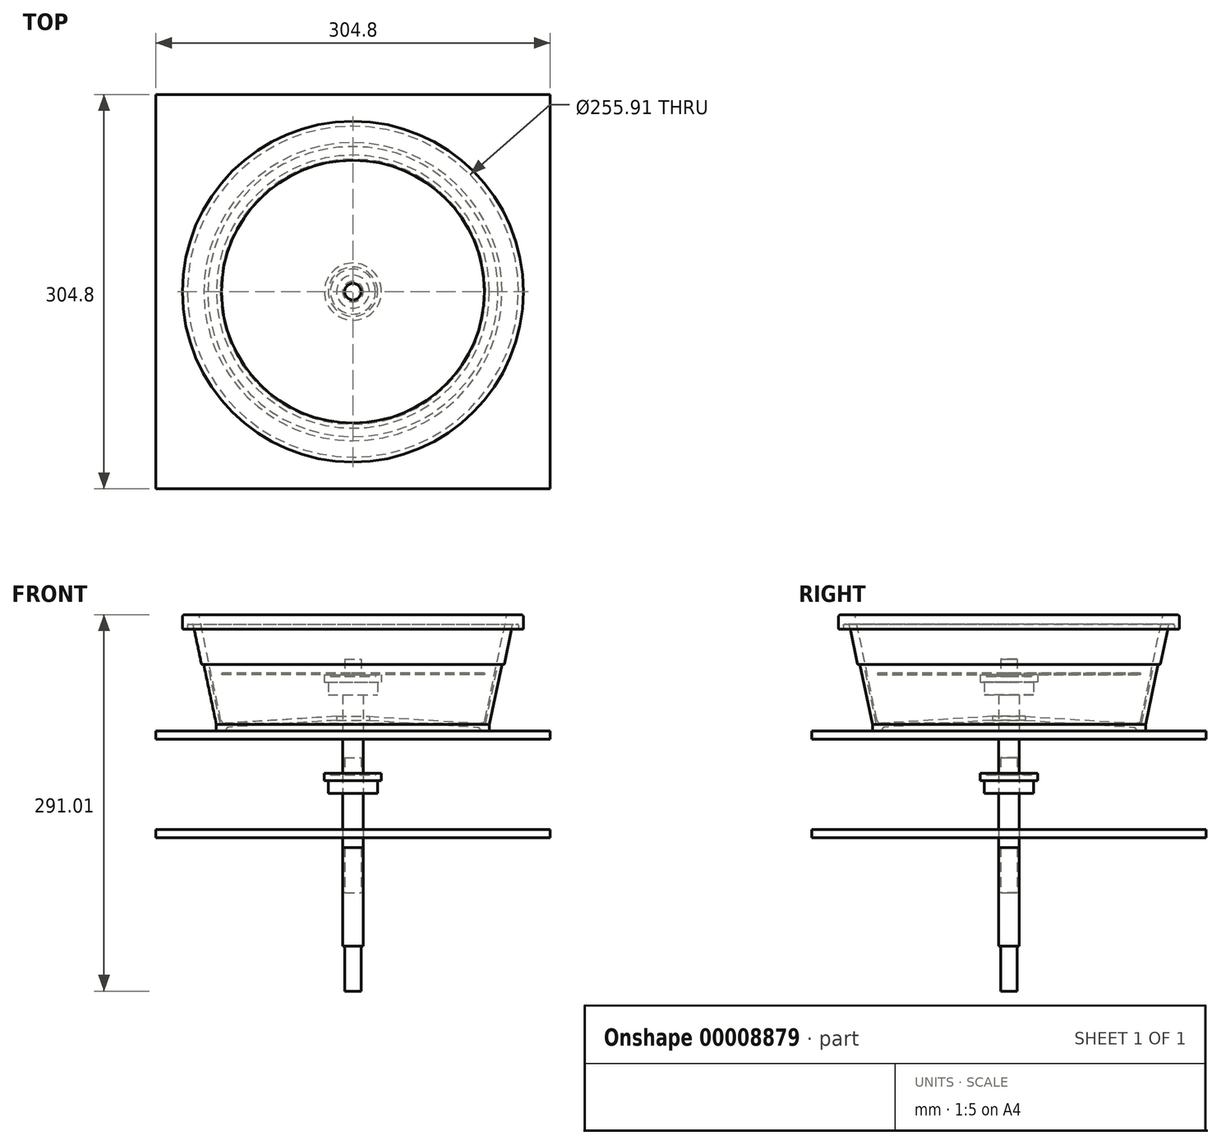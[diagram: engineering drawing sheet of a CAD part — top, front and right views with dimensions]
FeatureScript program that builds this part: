
annotation { "Feature Type Name" : "Feature", "Feature Type Description" : "" }
export const myFeature = defineFeature(function(context is Context, id is Id, definition is map)
    precondition{}
    {
        {
            var Q0;
            Q0=qCreatedBy(makeId("Front.planeOp"),FACE);
            var sketch = newSketch(context, id + "F0", { "sketchPlane" : qUnion([Q0])});
            skLineSegment(sketch, "E0", {"start": v(0, 0) * mm, "end": v(96.23, -6.08) * mm});
            skLineSegment(sketch, "E1", {"start": v(98.98, -8.76) * mm, "end": v(96.77, -6.33) * mm});
            skLineSegment(sketch, "E2", {"start": v(99.57, -9.02) * mm, "end": v(104.77, -9.02) * mm});
            skLineSegment(sketch, "E3", {"start": v(105.57, -8.22) * mm, "end": v(105.57, -3.94) * mm});
            skLineSegment(sketch, "E4", {"start": v(115.12, 41.79) * mm, "end": v(105.57, -3.94) * mm});
            skLineSegment(sketch, "E5", {"start": v(115.9, 42.42) * mm, "end": v(116.39, 42.42) * mm});
            skLineSegment(sketch, "E6", {"start": v(117.16, 43.05) * mm, "end": v(123.38, 72.77) * mm});
            skLineSegment(sketch, "E7", {"start": v(124.15, 73.4) * mm, "end": v(127.16, 73.4) * mm});
            skLineSegment(sketch, "E8", {"start": v(127.95, 72.61) * mm, "end": v(127.95, 70.39) * mm});
            skLineSegment(sketch, "E9", {"start": v(128.75, 69.6) * mm, "end": v(130.97, 69.6) * mm});
            skLineSegment(sketch, "E10", {"start": v(131.76, 70.39) * mm, "end": v(131.76, 79.18) * mm});
            skLineSegment(sketch, "E11", {"start": v(130.18, 80.77) * mm, "end": v(119.7, 80.77) * mm});
            skLineSegment(sketch, "E12", {"start": v(118.93, 80.14) * mm, "end": v(102.05, -0.66) * mm});
            skLineSegment(sketch, "E13", {"start": v(98.74, -3.18) * mm, "end": v(0, 3.05) * mm});
            skLineSegment(sketch, "E14", {"start": v(0, 3.05) * mm, "end": v(0, 0) * mm});
            skLineSegment(sketch, "E15", {"start": v(0, 0) * mm, "end": v(0, -9.02) * mm, "construction": true});
            skLineSegment(sketch, "E16", {"start": v(-105.57, -9.02) * mm, "end": v(105.57, -9.02) * mm, "construction": true});
            skLineSegment(sketch, "E17", {"start": v(0, 0) * mm, "end": v(0, 80.77) * mm, "construction": true});
            skLineSegment(sketch, "E18", {"start": v(-131.76, 80.77) * mm, "end": v(131.76, 80.77) * mm, "construction": true});
            skPoint(sketch, "E19.visualSharp", {"position": v(131.76, 80.77) * mm});
            skArc(sketch, "E19.filletArc", {"start": v(131.76, 79.18) * mm, "mid": v(131.3, 80.3) * mm, "end": v(130.18, 80.77) * mm});
            skPoint(sketch, "E20.visualSharp", {"position": v(119.06, 80.77) * mm});
            skArc(sketch, "E20.filletArc", {"start": v(119.7, 80.77) * mm, "mid": v(119.2, 80.6) * mm, "end": v(118.93, 80.14) * mm});
            skPoint(sketch, "E21.visualSharp", {"position": v(131.76, 69.6) * mm});
            skArc(sketch, "E21.filletArc", {"start": v(130.97, 69.6) * mm, "mid": v(131.53, 69.83) * mm, "end": v(131.76, 70.39) * mm});
            skPoint(sketch, "E22.visualSharp", {"position": v(127.95, 69.6) * mm});
            skArc(sketch, "E22.filletArc", {"start": v(127.95, 70.39) * mm, "mid": v(128.18, 69.83) * mm, "end": v(128.75, 69.6) * mm});
            skPoint(sketch, "E23.visualSharp", {"position": v(127.95, 73.4) * mm});
            skArc(sketch, "E23.filletArc", {"start": v(127.95, 72.61) * mm, "mid": v(127.72, 73.17) * mm, "end": v(127.16, 73.4) * mm});
            skPoint(sketch, "E24.visualSharp", {"position": v(123.5, 73.4) * mm});
            skArc(sketch, "E24.filletArc", {"start": v(124.15, 73.4) * mm, "mid": v(123.65, 73.23) * mm, "end": v(123.38, 72.77) * mm});
            skPoint(sketch, "E25.visualSharp", {"position": v(117.03, 42.42) * mm});
            skArc(sketch, "E25.filletArc", {"start": v(116.39, 42.42) * mm, "mid": v(116.89, 42.6) * mm, "end": v(117.16, 43.05) * mm});
            skPoint(sketch, "E26.visualSharp", {"position": v(115.25, 42.42) * mm});
            skArc(sketch, "E26.filletArc", {"start": v(115.9, 42.42) * mm, "mid": v(115.4, 42.24) * mm, "end": v(115.12, 41.79) * mm});
            skPoint(sketch, "E27.visualSharp", {"position": v(105.57, -9.02) * mm});
            skArc(sketch, "E27.filletArc", {"start": v(104.77, -9.02) * mm, "mid": v(105.34, -8.78) * mm, "end": v(105.57, -8.22) * mm});
            skPoint(sketch, "E28.visualSharp", {"position": v(99.22, -9.02) * mm});
            skArc(sketch, "E28.filletArc", {"start": v(98.98, -8.76) * mm, "mid": v(99.25, -8.95) * mm, "end": v(99.57, -9.02) * mm});
            skPoint(sketch, "E29.visualSharp", {"position": v(96.55, -6.1) * mm});
            skArc(sketch, "E29.filletArc", {"start": v(96.77, -6.33) * mm, "mid": v(96.52, -6.15) * mm, "end": v(96.23, -6.08) * mm});
            skPoint(sketch, "E30.visualSharp", {"position": v(101.48, -3.35) * mm});
            skArc(sketch, "E30.filletArc", {"start": v(98.74, -3.18) * mm, "mid": v(100.86, -2.54) * mm, "end": v(102.05, -0.66) * mm});
            skSolve(sketch);
        }
        {
            var Q0;
            Q0=makeQuery(id+"F0.imprint","IMPRINT",FACE,{"disambiguationData":[TD([[makeQuery(id+"F0.imprint","IMPRINT",EDGE,{"derivedFrom":sQuery(id+"F0.wireOp",EDGE,"E0")}),1.0]])]});
            var Q1;
            Q1=sQuery(id+"F0.wireOp",EDGE,"E17");
            revolve(context, id + "F1", {"entities" : qUnion([Q0]), "axis" : qUnion([Q1]), "revolveType" : RevolveType.FULL});
        }
        {
            var Q0;
            Q0=qCreatedBy(makeId("Front.planeOp"),FACE);
            var sketch = newSketch(context, id + "F2", { "sketchPlane" : qUnion([Q0])});
            skLineSegment(sketch, "E31", {"start": v(0, 0) * mm, "end": v(96.23, -6.08) * mm});
            skLineSegment(sketch, "E32", {"start": v(98.98, -8.76) * mm, "end": v(96.77, -6.33) * mm});
            skLineSegment(sketch, "E33", {"start": v(99.57, -9.02) * mm, "end": v(104.78, -9.02) * mm});
            skLineSegment(sketch, "E34", {"start": v(105.57, -8.22) * mm, "end": v(105.57, -3.94) * mm});
            skLineSegment(sketch, "E35", {"start": v(115.29, 42.42) * mm, "end": v(105.57, -3.94) * mm});
            skLineSegment(sketch, "E36", {"start": v(102.56, -3.42) * mm, "end": v(0, 3.05) * mm});
            skLineSegment(sketch, "E37", {"start": v(0, 3.05) * mm, "end": v(0, 0) * mm});
            skLineSegment(sketch, "E38", {"start": v(0, 0) * mm, "end": v(0, -9.02) * mm, "construction": true});
            skLineSegment(sketch, "E39", {"start": v(-105.57, -9.02) * mm, "end": v(105.57, -9.02) * mm, "construction": true});
            skLineSegment(sketch, "E40", {"start": v(0, 0) * mm, "end": v(0, 80.77) * mm, "construction": true});
            skPoint(sketch, "E41.visualSharp", {"position": v(105.57, -9.02) * mm});
            skArc(sketch, "E41.filletArc", {"start": v(104.78, -9.02) * mm, "mid": v(105.34, -8.78) * mm, "end": v(105.57, -8.22) * mm});
            skPoint(sketch, "E42.visualSharp", {"position": v(99.22, -9.02) * mm});
            skArc(sketch, "E42.filletArc", {"start": v(98.98, -8.76) * mm, "mid": v(99.25, -8.95) * mm, "end": v(99.57, -9.02) * mm});
            skPoint(sketch, "E43.visualSharp", {"position": v(96.55, -6.1) * mm});
            skArc(sketch, "E43.filletArc", {"start": v(96.77, -6.33) * mm, "mid": v(96.52, -6.15) * mm, "end": v(96.23, -6.08) * mm});
            skLineSegment(sketch, "E44", {"start": v(112.17, 42.42) * mm, "end": v(115.29, 42.42) * mm});
            skLineSegment(sketch, "E45", {"start": v(112.17, 42.42) * mm, "end": v(102.56, -3.42) * mm});
            skSolve(sketch);
        }
        {
            var Q0;
            Q0=makeQuery(id+"F2.imprint","IMPRINT",FACE,{"disambiguationData":[TD([[makeQuery(id+"F2.imprint","IMPRINT",EDGE,{"derivedFrom":sQuery(id+"F2.wireOp",EDGE,"E31")}),1.0]])]});
            var Q1;
            Q1=sQuery(id+"F2.wireOp",EDGE,"E40");
            revolve(context, id + "F3", {"entities" : qUnion([Q0]), "axis" : qUnion([Q1]), "revolveType" : RevolveType.FULL});
        }
        {
            var Q0;
            Q0=qCreatedBy(makeId("Top.planeOp"),FACE);
            var sketch = newSketch(context, id + "F4", { "sketchPlane" : qUnion([Q0])});
            skCircle(sketch, "E46", {"center": v(0, 0) * mm, "radius": 12.7 * mm});
            skSolve(sketch);
        }
        {
            var Q0;
            Q0=makeQuery(id+"F4.imprint","IMPRINT",FACE,{"disambiguationData":[TD([[makeQuery(id+"F4.imprint","IMPRINT",EDGE,{"derivedFrom":sQuery(id+"F4.wireOp",EDGE,"E46")}),1.0]])]});
            var Q1;
            Q1=sQuery(id+"F4.wireOp",EDGE,"E46");
            extrude(context, id + "F5", {"entities" : qUnion([Q0]), "operationType" : NewBodyOperationType.REMOVE, "surfaceEntities" : qUnion([Q1]), "endBound" : BoundingType.SYMMETRIC, "depth" : 25.4 * mm});
        }
        {
            var Q0;
            Q0=makeQuery(id+"F4.imprint","IMPRINT",FACE,{"disambiguationData":[TD([[makeQuery(id+"F4.imprint","IMPRINT",EDGE,{"derivedFrom":sQuery(id+"F4.wireOp",EDGE,"E46")}),1.0]])]});
            var Q1;
            Q1=sQuery(id+"F4.wireOp",EDGE,"E46");
            extrude(context, id + "F6", {"entities" : qUnion([Q0]), "operationType" : NewBodyOperationType.REMOVE, "surfaceEntities" : qUnion([Q1]), "endBound" : BoundingType.SYMMETRIC, "oppositeDirection" : true, "depth" : 25.4 * mm});
        }
        {
            var Q0;
            Q0=makeQuery(id+"F1.opRevolve","SWEPT_FACE",FACE,{"disambiguationData":[OSD([sQuery(id+"F0.wireOp",EDGE,"E2")])]});
            cPlane(context, id + "F7", {"entities" : qUnion([Q0]), "cplaneType" : CPlaneType.OFFSET, "offset" : 0 * mm, "width" : 152.4 * mm, "height" : 152.4 * mm});
        }
        {
            var Q0;
            Q0=qCreatedBy(id+"F7.planeOp",FACE);
            var sketch = newSketch(context, id + "F8", { "sketchPlane" : qUnion([Q0])});
            skLineSegment(sketch, "E47.rect.bottom", {"start": v(152.4, 152.4) * mm, "end": v(-152.4, 152.4) * mm});
            skLineSegment(sketch, "E47.rect.top", {"start": v(152.4, -152.4) * mm, "end": v(-152.4, -152.4) * mm});
            skLineSegment(sketch, "E47.rect.left", {"start": v(152.4, 152.4) * mm, "end": v(152.4, -152.4) * mm});
            skLineSegment(sketch, "E47.rect.right", {"start": v(-152.4, 152.4) * mm, "end": v(-152.4, -152.4) * mm});
            skPoint(sketch, "E47.rect.middle", {"position": v(0, 0) * mm});
            skCircle(sketch, "E48", {"center": v(0, 0) * mm, "radius": 7.94 * mm});
            skSolve(sketch);
        }
        {
            var Q0;
            Q0=makeQuery(id+"F8.imprint","IMPRINT",FACE,{"disambiguationData":[TD([[makeQuery(id+"F8.imprint","IMPRINT",EDGE,{"derivedFrom":sQuery(id+"F8.wireOp",EDGE,"E47.rect.bottom")}),1.0]])]});
            extrude(context, id + "F9", {"entities" : qUnion([Q0]), "depth" : 6.35 * mm});
        }
        {
            var Q0;
            Q0=qCreatedBy(makeId("Front.planeOp"),FACE);
            var sketch = newSketch(context, id + "F10", { "sketchPlane" : qUnion([Q0])});
            skLineSegment(sketch, "E49", {"start": v(0, -134.04) * mm, "end": v(0, 46.55) * mm});
            skLineSegment(sketch, "E50", {"start": v(-6.35, 46.55) * mm, "end": v(0, 46.55) * mm, "construction": true});
            skLineSegment(sketch, "E51", {"start": v(-6.35, 46.55) * mm, "end": v(-6.35, 33.06) * mm, "construction": true});
            skLineSegment(sketch, "E52", {"start": v(6.35, 33.06) * mm, "end": v(17.4, 33.06) * mm});
            skLineSegment(sketch, "E53", {"start": v(17.4, 33.06) * mm, "end": v(17.4, 34.41) * mm});
            skLineSegment(sketch, "E54", {"start": v(17.4, 34.41) * mm, "end": v(22.1, 34.41) * mm});
            skLineSegment(sketch, "E55", {"start": v(22.1, 34.41) * mm, "end": v(22.1, 28.57) * mm});
            skLineSegment(sketch, "E56", {"start": v(22.1, 28.57) * mm, "end": v(19.05, 28.57) * mm});
            skLineSegment(sketch, "E57", {"start": v(19.05, 28.57) * mm, "end": v(19.05, 19) * mm});
            skLineSegment(sketch, "E58", {"start": v(19.05, 19) * mm, "end": v(7.94, 19) * mm});
            skLineSegment(sketch, "E59", {"start": v(7.94, 19) * mm, "end": v(7.94, -99.12) * mm});
            skLineSegment(sketch, "E60", {"start": v(7.94, -99.12) * mm, "end": v(6.35, -99.12) * mm});
            skLineSegment(sketch, "E61", {"start": v(6.35, -99.12) * mm, "end": v(6.35, -134.04) * mm});
            skLineSegment(sketch, "E62", {"start": v(6.35, -134.04) * mm, "end": v(0, -134.04) * mm});
            skLineSegment(sketch, "E63.0.MirrorCS", {"start": v(-17.4, 33.06) * mm, "end": v(-17.4, 34.41) * mm, "construction": true});
            skLineSegment(sketch, "E63.1.MirrorCS", {"start": v(-7.94, -99.12) * mm, "end": v(-6.35, -99.12) * mm, "construction": true});
            skLineSegment(sketch, "E63.2.MirrorCS", {"start": v(-22.1, 34.41) * mm, "end": v(-22.1, 28.57) * mm, "construction": true});
            skLineSegment(sketch, "E63.3.MirrorCS", {"start": v(-22.1, 28.57) * mm, "end": v(-19.05, 28.57) * mm, "construction": true});
            skLineSegment(sketch, "E63.4.MirrorCS", {"start": v(6.35, 46.55) * mm, "end": v(6.35, 33.06) * mm});
            skLineSegment(sketch, "E63.5.MirrorCS", {"start": v(6.35, 46.55) * mm, "end": v(0, 46.55) * mm});
            skLineSegment(sketch, "E63.7.MirrorCS", {"start": v(-17.4, 34.41) * mm, "end": v(-22.1, 34.41) * mm, "construction": true});
            skLineSegment(sketch, "E63.8.MirrorCS", {"start": v(-6.35, -99.12) * mm, "end": v(-6.35, -134.04) * mm, "construction": true});
            skLineSegment(sketch, "E63.9.MirrorCS", {"start": v(-19.05, 28.57) * mm, "end": v(-19.05, 19) * mm, "construction": true});
            skLineSegment(sketch, "E63.10.MirrorCS", {"start": v(-19.05, 19) * mm, "end": v(-7.94, 19) * mm, "construction": true});
            skLineSegment(sketch, "E63.11.MirrorCS", {"start": v(-6.35, -134.04) * mm, "end": v(0, -134.04) * mm, "construction": true});
            skLineSegment(sketch, "E63.12.MirrorCS", {"start": v(-7.94, 19) * mm, "end": v(-7.94, -99.12) * mm, "construction": true});
            skLineSegment(sketch, "E64", {"start": v(-6.35, 33.06) * mm, "end": v(-17.4, 33.06) * mm, "construction": true});
            skSolve(sketch);
        }
        {
            var Q0;
            Q0=makeQuery(id+"F10.imprint","IMPRINT",FACE,{"disambiguationData":[TD([[makeQuery(id+"F10.imprint","IMPRINT",EDGE,{"derivedFrom":sQuery(id+"F10.wireOp",EDGE,"E49")}),-1.0]])]});
            var Q1;
            Q1=sQuery(id+"F10.wireOp",EDGE,"E49");
            revolve(context, id + "F11", {"entities" : qUnion([Q0]), "axis" : qUnion([Q1]), "revolveType" : RevolveType.FULL});
        }
        {
            var Q0;
            Q0=makeQuery(id+"F11.opRevolve","SWEPT_FACE",FACE,{"disambiguationData":[OSD([sQuery(id+"F10.wireOp",EDGE,"E54")])]});
            var sketch = newSketch(context, id + "F12", { "sketchPlane" : qUnion([Q0])});
            skCircle(sketch, "E65", {"center": v(0, 0) * mm, "radius": 6.35 * mm});
            skCircle(sketch, "E66", {"center": v(0, 0) * mm, "radius": 101.6 * mm});
            skSolve(sketch);
        }
        {
            var Q0;
            Q0=makeQuery(id+"F12.imprint","IMPRINT",FACE,{"disambiguationData":[TD([[makeQuery(id+"F12.imprint","IMPRINT",EDGE,{"derivedFrom":sQuery(id+"F12.wireOp",EDGE,"E66")}),1.0]])]});
            var Q1;
            {var subQ0=sQuery(id+"F10.wireOp",EDGE,"E54");Q1=makeQuery(id+"F12.imprint","IMPRINT",FACE,{"disambiguationData":[TD([[makeQuery(id+"F12.imprint","IMPRINT",EDGE,{"derivedFrom":makeQuery(id+"F11.opRevolve","SWEPT_EDGE",EDGE,{"disambiguationData":[OSD([sQuery(id+"F10.wireOp",EDGE,"E53"),subQ0])]})}),1.0]])]});}
            var Q2;
            Q2=makeQuery(id+"F12.imprint","IMPRINT",FACE,{"disambiguationData":[TD([[makeQuery(id+"F12.imprint","IMPRINT",EDGE,{"derivedFrom":sQuery(id+"F12.wireOp",EDGE,"E65")}),-1.0]])]});
            extrude(context, id + "F13", {"entities" : qUnion([Q0, Q1, Q2]), "depth" : 1.27 * mm});
        }
        {
            var Q0;
            Q0=makeQuery(id+"F9.opExtrude","CAP_FACE",FACE,{"disambiguationData":[OSD([sQuery(id+"F8.wireOp",EDGE,"E47.rect.bottom"),sQuery(id+"F8.wireOp",EDGE,"E47.rect.top"),sQuery(id+"F8.wireOp",EDGE,"E47.rect.left"),sQuery(id+"F8.wireOp",EDGE,"E47.rect.right"),sQuery(id+"F8.wireOp",EDGE,"E48")])],"isStart":true});
            var sketch = newSketch(context, id + "F14", { "sketchPlane" : qUnion([Q0])});
            skCircle(sketch, "E67", {"center": v(0, 0) * mm, "radius": 19.05 * mm});
            skCircle(sketch, "E68", {"center": v(0, 0) * mm, "radius": 7.94 * mm});
            skCircle(sketch, "E69", {"center": v(0, 0) * mm, "radius": 17.46 * mm});
            skCircle(sketch, "E70", {"center": v(0, 0) * mm, "radius": 11.66 * mm});
            skSolve(sketch);
        }
        {
            var Q0;
            Q0=makeQuery(id+"F14.imprint","IMPRINT",FACE,{"disambiguationData":[TD([[makeQuery(id+"F14.imprint","IMPRINT",EDGE,{"derivedFrom":sQuery(id+"F14.wireOp",EDGE,"E68")}),-1.0]])]});
            extrude(context, id + "F15", {"entities" : qUnion([Q0]), "depth" : 3.17 * mm});
        }
        {
            var Q0;
            Q0=makeQuery(id+"F14.imprint","IMPRINT",FACE,{"disambiguationData":[TD([[makeQuery(id+"F14.imprint","IMPRINT",EDGE,{"derivedFrom":sQuery(id+"F14.wireOp",EDGE,"E67")}),1.0]])]});
            var Q1;
            Q1=makeQuery(id+"F14.imprint","IMPRINT",FACE,{"disambiguationData":[TD([[makeQuery(id+"F14.imprint","IMPRINT",EDGE,{"derivedFrom":sQuery(id+"F14.wireOp",EDGE,"E69")}),-1.0]])]});
            extrude(context, id + "F16", {"entities" : qUnion([Q0, Q1]), "operationType" : NewBodyOperationType.ADD, "depth" : 1 / 406.4 * mm});
        }
        {
            var Q0;
            Q0=makeQuery(id+"F14.imprint","IMPRINT",FACE,{"disambiguationData":[TD([[makeQuery(id+"F14.imprint","IMPRINT",EDGE,{"derivedFrom":sQuery(id+"F14.wireOp",EDGE,"E68")}),-1.0]])]});
            var Q1;
            Q1=makeQuery(id+"F14.imprint","IMPRINT",FACE,{"disambiguationData":[TD([[makeQuery(id+"F14.imprint","IMPRINT",EDGE,{"derivedFrom":sQuery(id+"F14.wireOp",EDGE,"E69")}),-1.0]])]});
            extrude(context, id + "F17", {"entities" : qUnion([Q0, Q1]), "operationType" : NewBodyOperationType.ADD, "oppositeDirection" : true, "depth" : 3 / 203.2 * mm});
        }
        {
            var Q0;
            Q0=makeQuery(id+"F15.opExtrude","SWEPT_BODY",BODY,{"disambiguationData":[OSD([sQuery(id+"F14.wireOp",EDGE,"E68"),sQuery(id+"F14.wireOp",EDGE,"E70")])]});
            var Q1;
            Q1=makeQuery(id+"F9.opExtrude","SWEPT_BODY",BODY,{"disambiguationData":[OSD([sQuery(id+"F8.wireOp",EDGE,"E47.rect.bottom"),sQuery(id+"F8.wireOp",EDGE,"E47.rect.top"),sQuery(id+"F8.wireOp",EDGE,"E47.rect.left"),sQuery(id+"F8.wireOp",EDGE,"E47.rect.right"),sQuery(id+"F8.wireOp",EDGE,"E48")])]});
            var Q2;
            Q2=makeQuery(id+"F11.opRevolve","SWEPT_FACE",FACE,{"disambiguationData":[OSD([sQuery(id+"F10.wireOp",EDGE,"E59")])]});
            transform(context, id + "F18", {"entities" : qUnion([Q0, Q1]), "transformType" : TransformType.TRANSLATION_DISTANCE, "transformDirection" : qUnion([Q2]), "distance" : 76.2 * mm, "makeCopy" : true});
        }
    });
